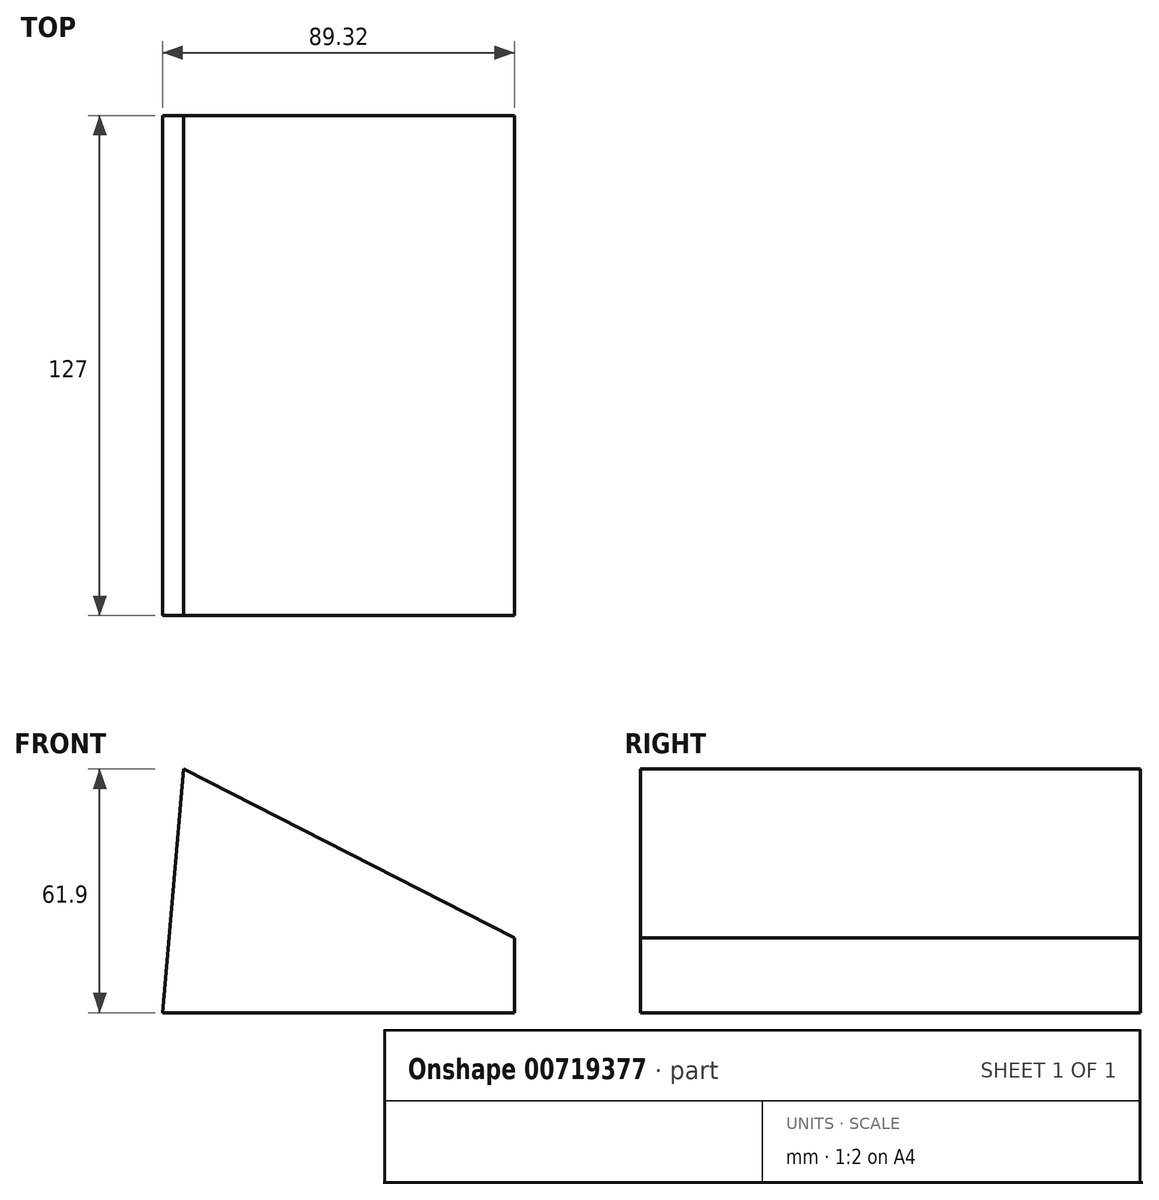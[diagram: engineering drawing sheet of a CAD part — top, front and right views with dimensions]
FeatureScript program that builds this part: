
annotation { "Feature Type Name" : "Feature", "Feature Type Description" : "" }
export const myFeature = defineFeature(function(context is Context, id is Id, definition is map)
    precondition{}
    {
        {
            var Q0;
            Q0=qCreatedBy(makeId("Front.planeOp"),FACE);
            var sketch = newSketch(context, id + "F0", { "sketchPlane" : qUnion([Q0])});
            skLineSegment(sketch, "E0", {"start": v(-40.96, 42.95) * mm, "end": v(43.13, 0) * mm});
            skLineSegment(sketch, "E1", {"start": v(43.13, 0) * mm, "end": v(43.13, -18.95) * mm});
            skLineSegment(sketch, "E2", {"start": v(43.13, -18.95) * mm, "end": v(-46.2, -18.95) * mm});
            skLineSegment(sketch, "E3", {"start": v(-46.2, -18.95) * mm, "end": v(-40.96, 42.95) * mm});
            skSolve(sketch);
        }
        {
            var Q0;
            Q0 = qSketchRegion(id + "F0", true);
            extrude(context, id + "F1", {"entities" : qUnion([Q0]), "depth" : 127 * mm, "offsetDistance" : 25.4 * mm});
        }
    });
